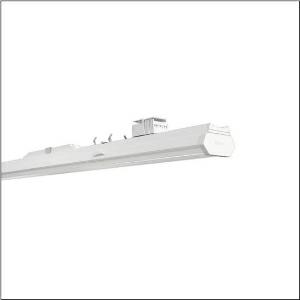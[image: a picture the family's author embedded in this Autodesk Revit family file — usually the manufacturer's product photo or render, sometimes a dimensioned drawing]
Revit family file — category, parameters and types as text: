
# Revit family: licross_21_protected_ho_52td11dn4e5s
name_source: partatom
category: Lighting Fixtures
units: mm (PartAtom-declared; Revit-internal decimal feet)

## family parameters
Cut with Voids When Loaded = No
Host = Face
Light Source = No
Part Type = Normal
Room Calculation Point = No
Round Connector Dimension = Use Diameter
Shared = No

## types (1)
- --- (1 x LED, 14920 lm, 84.9 W, 4000K)
    Apparent Load = 85 VA
    CIE Flux Codes = 84 94 98 99 100
    Color Rendering = 80
    Color Temperature = 4000K
    Default Elevation = 1800 mm
    Description = Licross 21 Protected HO, luminaire insert, of sheet steel, galvanised, coil coated, white, length: 1.500mm, width: 90mm, height: 103mm, LED rated luminous flux: 14.920lm, light colour: 840, SDCM (Standard Deviation of Colour Matching)MacAdam ≤ 3 SDCM (initial), control gear: DALI 2, with plug, 5-pole, with phase selection, mains connection: 220..240V, AC, 50/60Hz, rated input power: 85W, internal wiring halogen-free, primary light control with lens, of plastic, primary optical cover: cover, of PMMA, light emission: direct distribution, primary light characteristic: symmetric, protection rating (complete): IP54, insulation class (complete): insulation class I (protective earthing), certification: CE, ENEC, VDE, UKCA, protection symbol: D if used in an environment with non-conductive dust loads with corresponding accessories, impact resistance: IK06, permissible ambient temperature for indoor applications: -25..+35°C, corresponds to IFS (International Featured Standards) requirements for safety and quality in the food industry, reducing of maximum allowable ambient temperature of 5°C with ceiling mounting, LABS conformity tested according to VDMA 24364:2018-05, The light source and the operating device comply with the requirements of the Ecodesign Regulation (EU) 2019/2020 and are replaceable in accordance with this regulation, packaging unit: 1 piece
    Height = 92 mm
    Lamp = 1 x LED
    Lamp Light Flux = 14920 lm
    Lamp Power = 84.9 W
    Lamp count = 1
    Length = 1500 mm
    Luminous efficacy = 176 lm/W
    Manufacturer = Siteco
    ModVariant = No
    Model = 52TD11DN4E5S
    Mounting Place = Ceiling
    Mounting Type = Pendant
    Number of Poles = 1
    OnlyDefault = Yes
    Power Factor = 1
    Product Name = Licross 21 Protected HO
    Product group = luminaire insert | ceiling pendant
    ProductGroupID = 901
    Protection Class = Protection class I
    Protection Degree = IP 54
    RLX_Detail_Level = 1
    RLX_Emergency_Light_Flux = 0 lm
    RLX_Emergency_Type = 0
    RLX_Emergency_Type_DB = No
    RlxData = <blob elided: 24661 chars, md5=1f65a681>
    Socket = socket
    Standby Power = 0 W
    System Light Flux = 14920 lm
    System Power = 85 W
    Type Comments = factory setting: luminous flux: 100 % | dim-lin: 254 | 484 mA
    Type Image = l_1256148.jpg
    URL = http://relux.com
    VarID = @adj_128715
    Voltage = 0 V
    Weight = 0.00 kg
    Width = 88 mm

## geometry (parser evidence)
native form markers: Blend x4, Sweep x11
no freeform markers — native parametric forms only
